# Revit family: Building-FlushMountingEnclosures-GEWISS-24SC-GREENWALL-BOXES_3P
name_source: partatom
category: Apparecchi elettrici
revit_build: Autodesk Revit 2016 (Build: 20161004_0715(x64)
units: mm (PartAtom-declared; Revit-internal decimal feet)

## family parameters
Condiviso = Sì
Host = Superficie
Mantenere orientamento annotazione = Sì
Numero OmniClass = 23.80.30.14.24
Punto di calcolo locali = Sì
Quota connettore circolare = Usa diametro
Taglio con vuoti quando caricato = Sì
Tipo di parte = Normale
Titolo OmniClass = Junction Boxes

## types (1)
- GW24403PM - Halogen free - 3P
    Catalogue = BUILDING
    Catalogue Range = 24SC
    Description: = 3 gang
    Descrizione = PLASTERBOARD W. 3 GANG F.M.BOX - GW
    EAN code = 8011564801912
    Electrocod = 0210
    GW - Caratteristiche = Halogen free
    GW - Dim. esterne BxHxP (mm) = 110x73x50
    GW - Installazione = Flush mounting enclosures
    GW - Interasse fissaggio supporti = 83,5MM
    GW - N. moduli SYSTEM = 3 gang
    GW - Per Pareti = Plasterboard
    GW - Predisposizione scomparti = 2
    GW - Temperatura di impiego = -15 ÷ +60°C
    GW - Tipo Materiale = Halogen free with Standard EN 50267-2-2
    Glow Wire Test = 850°C
    IDF = 557917f4-c3e3-461a-bacb-7edae8bcb410
    IDT = 7e9ebd6a-1061-4bfe-9397-917a2868acc8
    IP degree = IP40
    Immagine tipo = GW24403PM.jpg
    Modello = GW24403PM
    Produttore = GEWISS S.p.A.
    Prospetto di default = 1219 mm
    SEO = Box
    Shock resistance = IK07
    Technical sheet = https://www.gewiss.com
    Thermo-pressure with ball = 70
    Type: = High capacity
    URL = https://www.gewiss.com
    Version file RFA = 19.0

note: source unit labels omitted for Thermo-pressure with ball — the stored unit's dimension contradicts the parameter name (converter mislabeling)

## geometry (parser evidence)
native form markers: Blend x4, Sweep x3
no freeform markers — native parametric forms only
